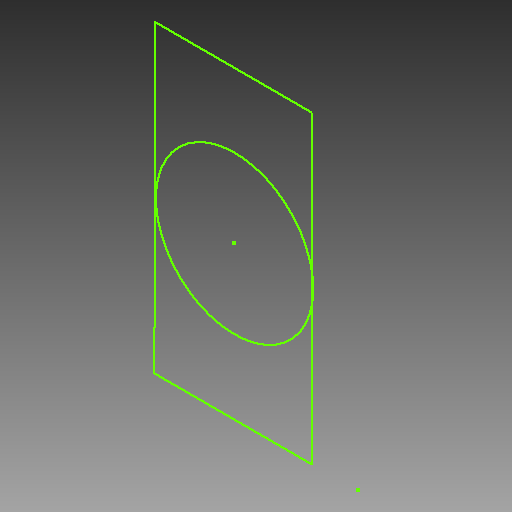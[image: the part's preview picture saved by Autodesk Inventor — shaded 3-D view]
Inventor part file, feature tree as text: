
AUTODESK INVENTOR PART (.ipt)
format: ipt  version: 2018 (Build 220112000, 112)  size: 68,096 bytes
history: native  units: in
note: dims shown in document units (in); Inventor stores cm internally (conversion verified against a paired STEP export)
features: sketch x1
ambient origin geometry x8: Origin, YZ Plane, XZ Plane, XY Plane, X Axis, Y Axis, Z Axis, Center Point
feature tree (1):
  sketch  "Sketch1"
